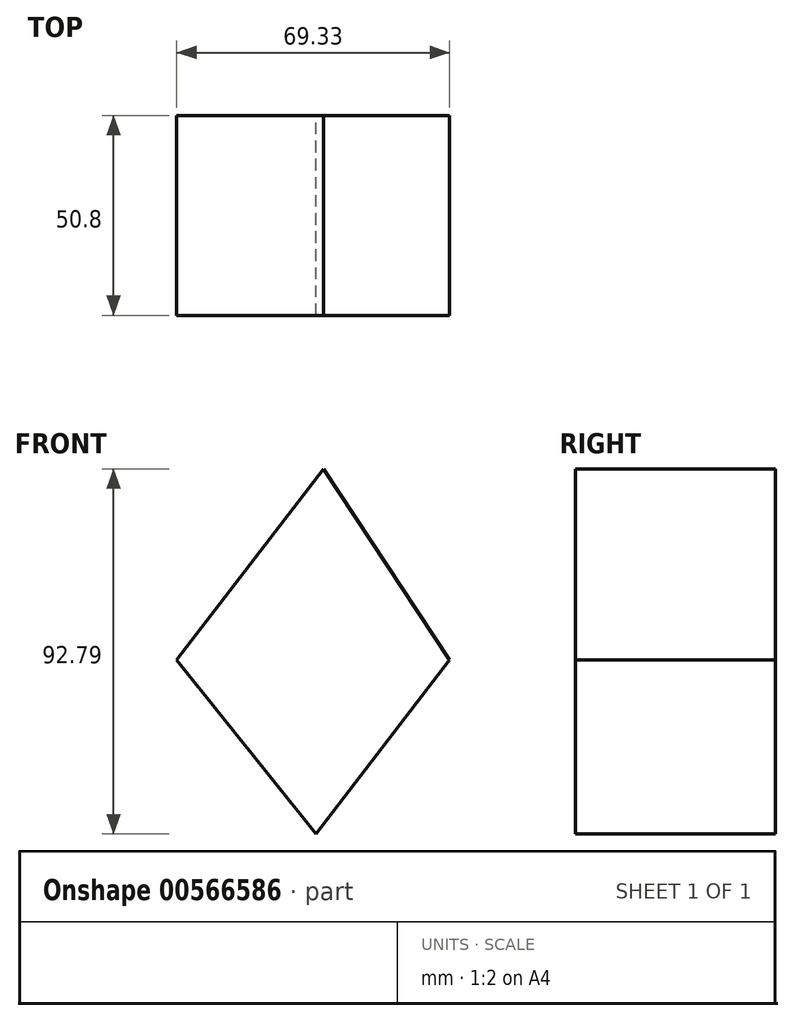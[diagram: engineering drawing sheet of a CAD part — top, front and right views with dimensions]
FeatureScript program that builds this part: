
annotation { "Feature Type Name" : "Feature", "Feature Type Description" : "" }
export const myFeature = defineFeature(function(context is Context, id is Id, definition is map)
    precondition{}
    {
        {
            var Q0;
            Q0=qCreatedBy(makeId("Front.planeOp"),FACE);
            var sketch = newSketch(context, id + "F0", { "sketchPlane" : qUnion([Q0])});
            skLineSegment(sketch, "E0", {"start": v(-37.26, 0) * mm, "end": v(0, 48.56) * mm});
            skLineSegment(sketch, "E1", {"start": v(0, 48.56) * mm, "end": v(32.07, 0) * mm});
            skLineSegment(sketch, "E2", {"start": v(32.07, 0) * mm, "end": v(-1.87, -44.23) * mm});
            skLineSegment(sketch, "E3", {"start": v(-37.26, 0) * mm, "end": v(-1.87, -44.23) * mm});
            skSolve(sketch);
        }
        {
            var Q0;
            Q0 = qSketchRegion(id + "F0", true);
            extrude(context, id + "F1", {"entities" : qUnion([Q0]), "depth" : 50.8 * mm, "offsetDistance" : 25.4 * mm});
        }
    });
